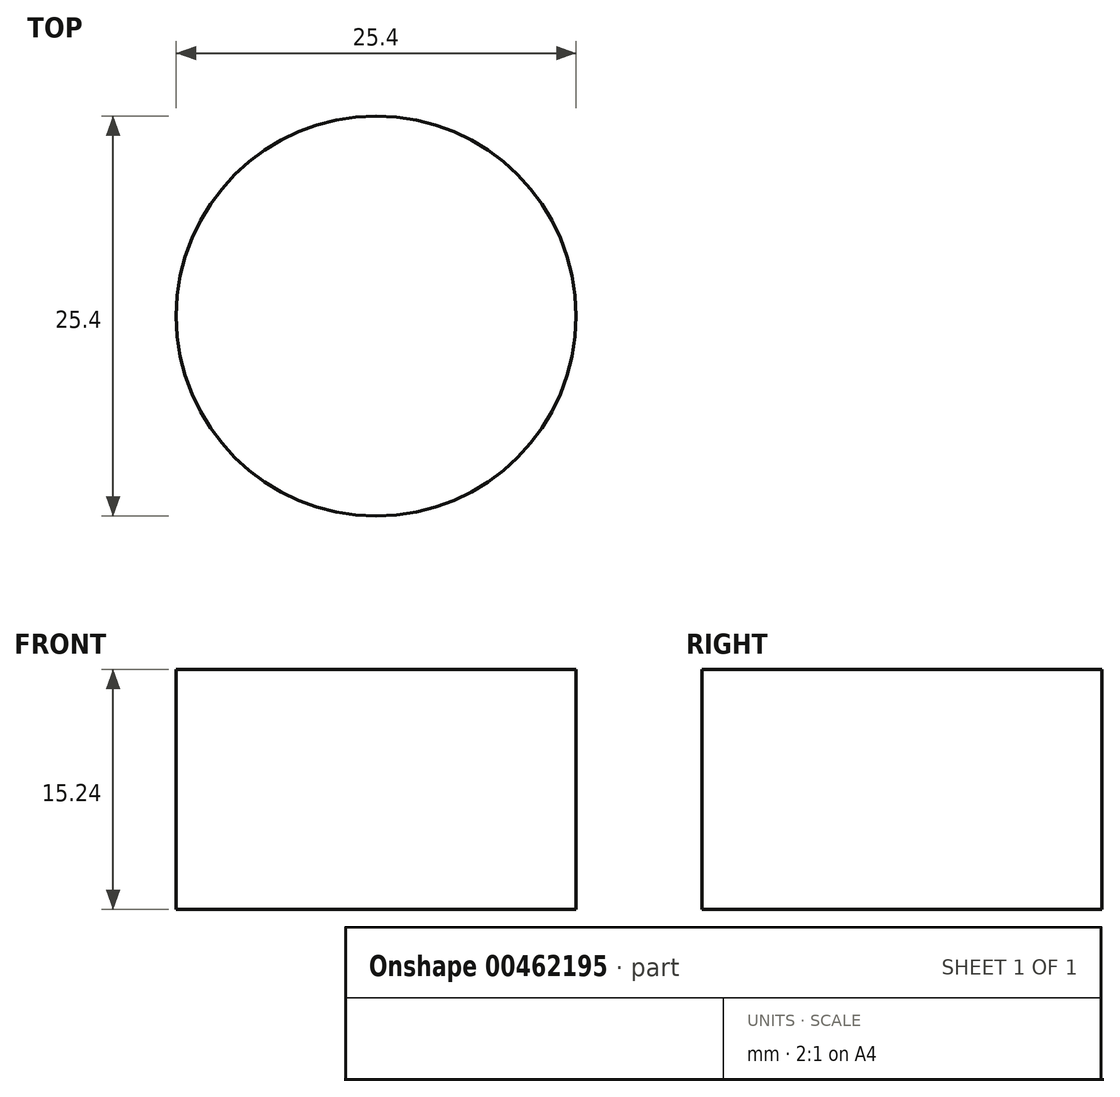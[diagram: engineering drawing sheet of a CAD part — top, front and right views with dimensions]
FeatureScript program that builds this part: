
annotation { "Feature Type Name" : "Feature", "Feature Type Description" : "" }
export const myFeature = defineFeature(function(context is Context, id is Id, definition is map)
    precondition{}
    {
        {
            var Q0;
            Q0=qCreatedBy(makeId("Top.planeOp"),FACE);
            var sketch = newSketch(context, id + "F0", { "sketchPlane" : qUnion([Q0])});
            skCircle(sketch, "E0", {"center": v(0, 0) * mm, "radius": 12.7 * mm});
            skSolve(sketch);
        }
        {
            var Q0;
            Q0 = qSketchRegion(id + "F0", true);
            extrude(context, id + "F1", {"entities" : qUnion([Q0]), "depth" : 15.24 * mm, "offsetDistance" : 25.4 * mm});
        }
    });
